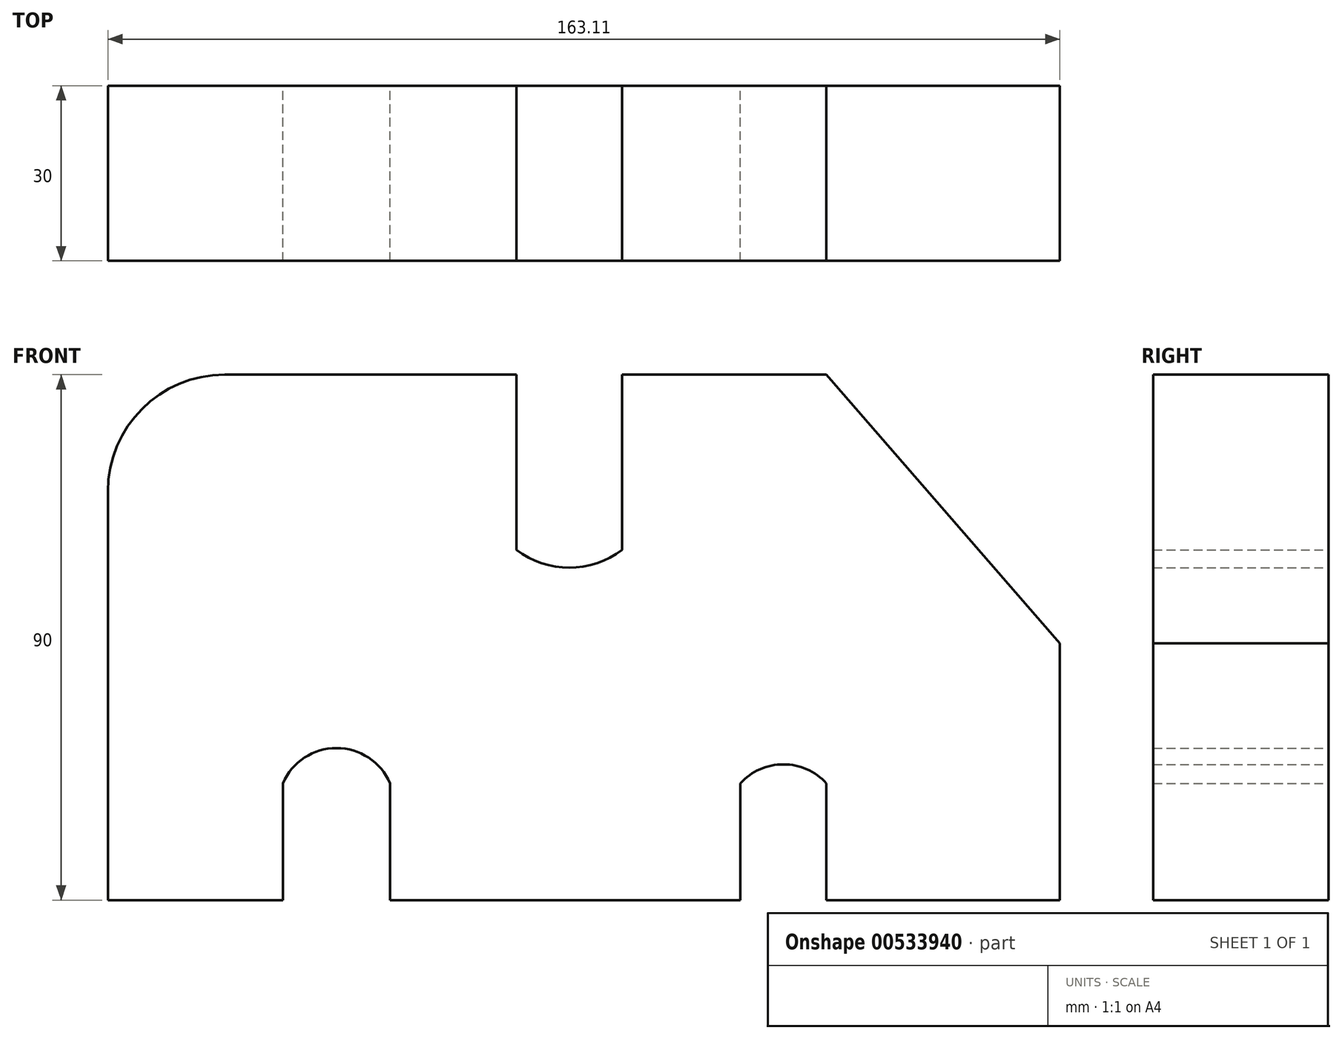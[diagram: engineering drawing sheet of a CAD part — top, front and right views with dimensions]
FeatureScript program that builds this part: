
annotation { "Feature Type Name" : "Feature", "Feature Type Description" : "" }
export const myFeature = defineFeature(function(context is Context, id is Id, definition is map)
    precondition{}
    {
        {
            var Q0;
            Q0=qCreatedBy(makeId("Front.planeOp"),FACE);
            var sketch = newSketch(context, id + "F0", { "sketchPlane" : qUnion([Q0])});
            skLineSegment(sketch, "E0", {"start": v(-11.8, 50.65) * mm, "end": v(-61.8, 50.65) * mm});
            skLineSegment(sketch, "E1", {"start": v(-81.8, 30.65) * mm, "end": v(-81.8, -39.35) * mm});
            skLineSegment(sketch, "E2", {"start": v(-81.8, -39.35) * mm, "end": v(-51.8, -39.35) * mm});
            skLineSegment(sketch, "E3", {"start": v(-51.8, -39.35) * mm, "end": v(-51.8, -19.35) * mm});
            skLineSegment(sketch, "E4", {"start": v(-33.45, -19.35) * mm, "end": v(-33.45, -39.35) * mm});
            skLineSegment(sketch, "E5", {"start": v(-33.45, -39.35) * mm, "end": v(26.55, -39.35) * mm});
            skLineSegment(sketch, "E6", {"start": v(26.55, -39.35) * mm, "end": v(26.55, -19.35) * mm});
            skLineSegment(sketch, "E7", {"start": v(41.3, -19.35) * mm, "end": v(41.3, -39.35) * mm});
            skLineSegment(sketch, "E8", {"start": v(41.3, -39.35) * mm, "end": v(81.3, -39.35) * mm});
            skLineSegment(sketch, "E9", {"start": v(81.3, -39.35) * mm, "end": v(81.3, 4.65) * mm});
            skLineSegment(sketch, "E10", {"start": v(81.3, 4.65) * mm, "end": v(41.3, 50.65) * mm});
            skLineSegment(sketch, "E11", {"start": v(41.3, 50.65) * mm, "end": v(6.3, 50.65) * mm});
            skLineSegment(sketch, "E12", {"start": v(6.3, 50.65) * mm, "end": v(6.3, 20.65) * mm});
            skLineSegment(sketch, "E13", {"start": v(-11.8, 20.65) * mm, "end": v(-11.8, 50.65) * mm});
            skPoint(sketch, "E14.visualSharp", {"position": v(-81.8, 50.65) * mm});
            skArc(sketch, "E14.filletArc", {"start": v(-61.8, 50.65) * mm, "mid": v(-75.95, 44.8) * mm, "end": v(-81.8, 30.65) * mm});
            skArc(sketch, "E15", {"start": v(-33.45, -19.35) * mm, "mid": v(-42.63, -13.32) * mm, "end": v(-51.8, -19.35) * mm});
            skPoint(sketch, "E16.start.orphan", {"position": v(-51.8, -6.17) * mm});
            skArc(sketch, "E17", {"start": v(41.3, -19.35) * mm, "mid": v(33.93, -16.1) * mm, "end": v(26.55, -19.35) * mm});
            skPoint(sketch, "E18.start.orphan", {"position": v(26.55, -6.17) * mm});
            skPoint(sketch, "E19.orphan", {"position": v(41.3, -16.22) * mm});
            skArc(sketch, "E20", {"start": v(-11.8, 20.65) * mm, "mid": v(-2.75, 17.6) * mm, "end": v(6.3, 20.65) * mm});
            skPoint(sketch, "E21.start.orphan", {"position": v(-11.8, 10.28) * mm});
            skPoint(sketch, "E22.orphan", {"position": v(6.3, 10.28) * mm});
            skSolve(sketch);
        }
        {
            var Q0;
            Q0=makeQuery(id+"F0.imprint","IMPRINT",FACE,{"disambiguationData":[TD([[makeQuery(id+"F0.imprint","IMPRINT",EDGE,{"derivedFrom":sQuery(id+"F0.wireOp",EDGE,"E0")}),1.0]])]});
            extrude(context, id + "F1", {"entities" : qUnion([Q0]), "depth" : 30 * mm, "offsetDistance" : 25 * mm});
        }
    });
